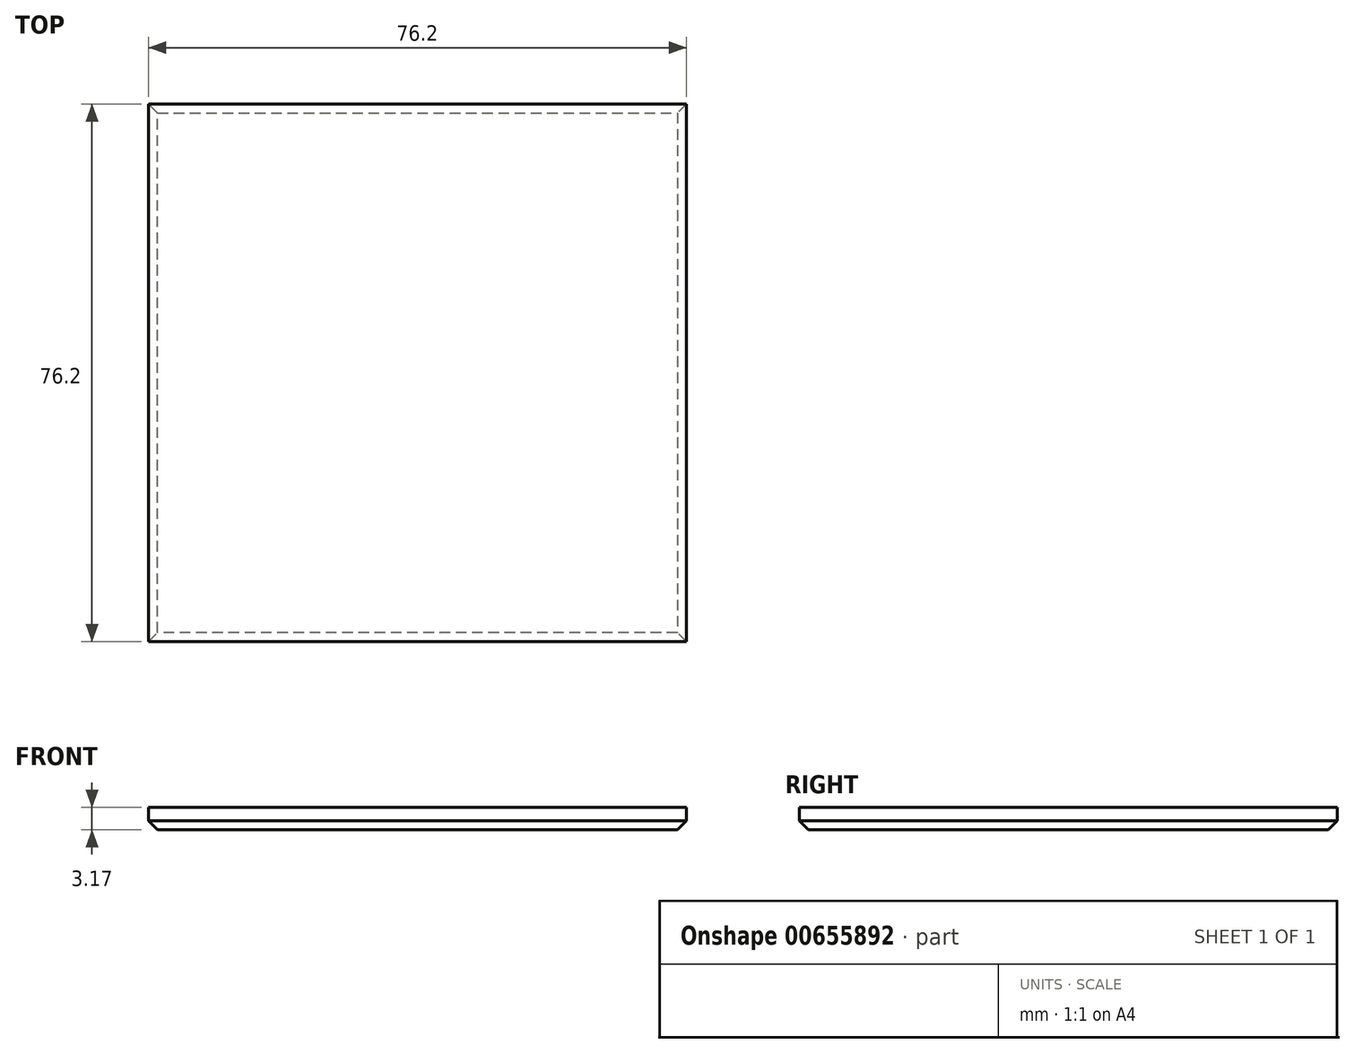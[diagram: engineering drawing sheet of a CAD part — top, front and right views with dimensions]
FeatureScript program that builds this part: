
annotation { "Feature Type Name" : "Feature", "Feature Type Description" : "" }
export const myFeature = defineFeature(function(context is Context, id is Id, definition is map)
    precondition{}
    {
        {
            var Q0;
            Q0=qCreatedBy(makeId("Top.planeOp"),FACE);
            var sketch = newSketch(context, id + "F0", { "sketchPlane" : qUnion([Q0])});
            skLineSegment(sketch, "E0.bottom", {"start": v(-38.1, -38.1) * mm, "end": v(38.1, -38.1) * mm});
            skLineSegment(sketch, "E0.top", {"start": v(-38.1, 38.1) * mm, "end": v(38.1, 38.1) * mm});
            skLineSegment(sketch, "E0.left", {"start": v(-38.1, -38.1) * mm, "end": v(-38.1, 38.1) * mm});
            skLineSegment(sketch, "E0.right", {"start": v(38.1, -38.1) * mm, "end": v(38.1, 38.1) * mm});
            skPoint(sketch, "E0.middle", {"position": v(0, 0) * mm});
            skSolve(sketch);
        }
        {
            var Q0;
            Q0=makeQuery(id+"F0.imprint","IMPRINT",FACE,{"disambiguationData":[TD([[makeQuery(id+"F0.imprint","IMPRINT",EDGE,{"derivedFrom":sQuery(id+"F0.wireOp",EDGE,"E0.bottom")}),1.0]])]});
            extrude(context, id + "F1", {"entities" : qUnion([Q0]), "depth" : 3.17 * mm, "offsetDistance" : 25.4 * mm});
        }
        {
            var Q0;
            Q0=makeQuery(id+"F1.opExtrude","CAP_EDGE",EDGE,{"disambiguationData":[OSD([sQuery(id+"F0.wireOp",EDGE,"E0.right")])],"isStart":true});
            chamfer(context, id + "F2", {"entities" : qUnion([Q0]), "width" : 1.27 * mm, "tangentPropagation" : true});
        }
        {
            var Q0;
            Q0=makeQuery(id+"F1.opExtrude","CAP_EDGE",EDGE,{"disambiguationData":[OSD([sQuery(id+"F0.wireOp",EDGE,"E0.top")])],"isStart":true});
            chamfer(context, id + "F3", {"entities" : qUnion([Q0]), "width" : 1.27 * mm, "tangentPropagation" : true});
        }
        {
            var Q0;
            Q0=makeQuery(id+"F1.opExtrude","CAP_EDGE",EDGE,{"disambiguationData":[OSD([sQuery(id+"F0.wireOp",EDGE,"E0.left")])],"isStart":true});
            chamfer(context, id + "F4", {"entities" : qUnion([Q0]), "width" : 1.27 * mm, "tangentPropagation" : true});
        }
        {
            var Q0;
            Q0=makeQuery(id+"F1.opExtrude","CAP_EDGE",EDGE,{"disambiguationData":[OSD([sQuery(id+"F0.wireOp",EDGE,"E0.bottom")])],"isStart":true});
            chamfer(context, id + "F5", {"entities" : qUnion([Q0]), "width" : 1.27 * mm, "tangentPropagation" : true});
        }
    });
